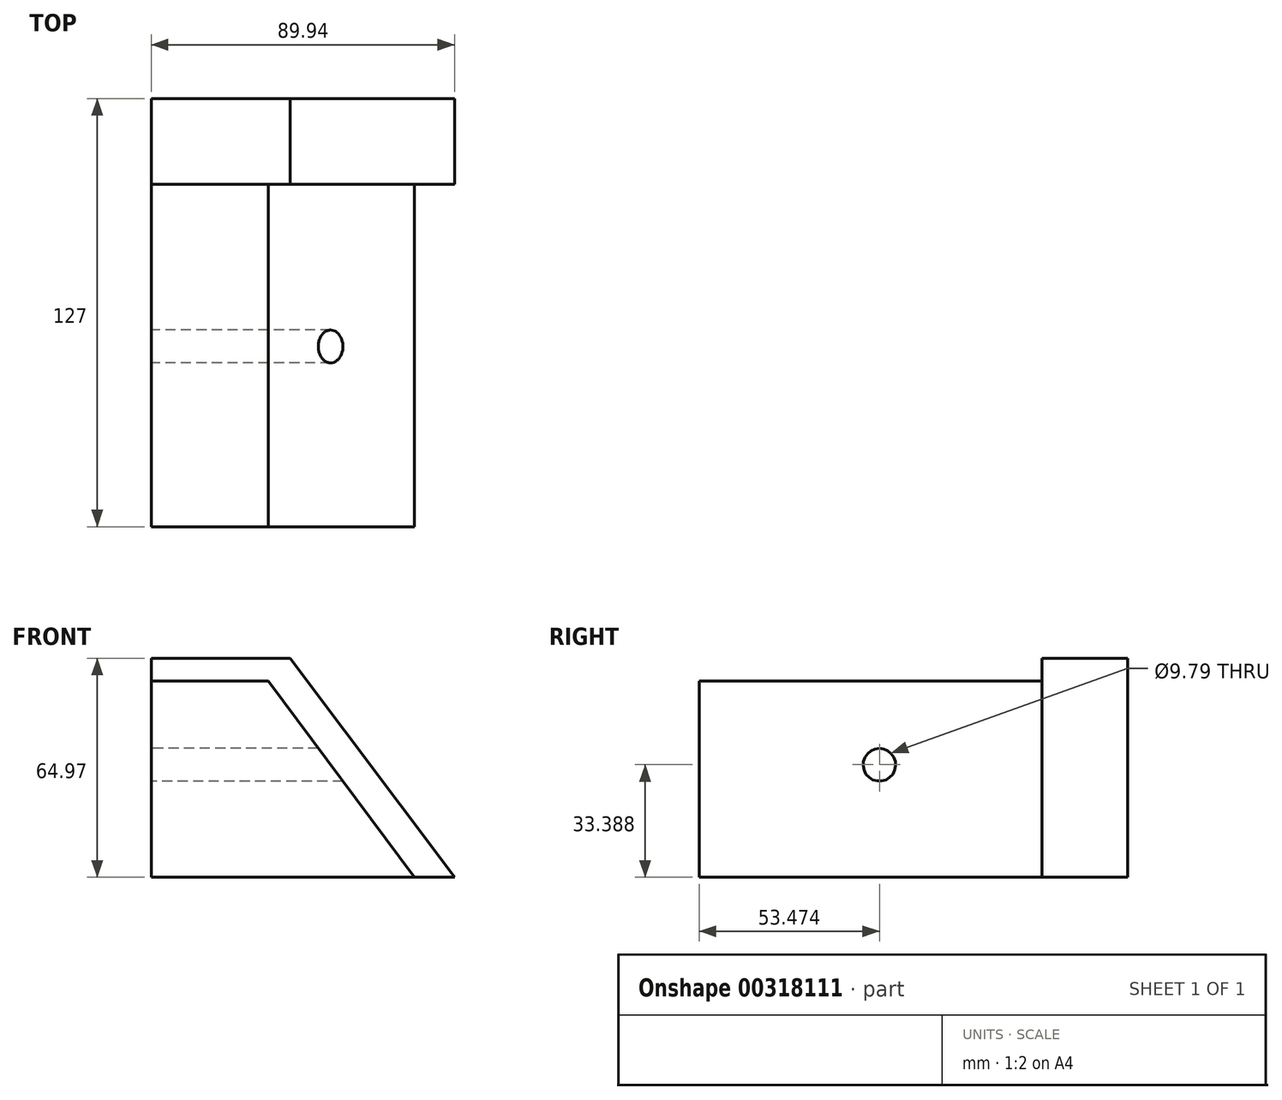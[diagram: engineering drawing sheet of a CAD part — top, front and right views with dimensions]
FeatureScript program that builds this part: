
annotation { "Feature Type Name" : "Feature", "Feature Type Description" : "" }
export const myFeature = defineFeature(function(context is Context, id is Id, definition is map)
    precondition{}
    {
        {
            var Q0;
            Q0=qCreatedBy(makeId("Front.planeOp"),FACE);
            var sketch = newSketch(context, id + "F0", { "sketchPlane" : qUnion([Q0])});
            skLineSegment(sketch, "E0.bottom", {"start": v(-64.07, 0) * mm, "end": v(25.87, 0) * mm});
            skLineSegment(sketch, "E0.top", {"start": v(-64.07, 64.97) * mm, "end": v(-22.86, 64.97) * mm});
            skLineSegment(sketch, "E0.left", {"start": v(-64.07, 0) * mm, "end": v(-64.07, 64.97) * mm});
            skLineSegment(sketch, "E1", {"start": v(25.87, 0) * mm, "end": v(-22.86, 64.97) * mm});
            skSolve(sketch);
        }
        {
            var Q0;
            Q0 = qSketchRegion(id + "F0", true);
            extrude(context, id + "F1", {"entities" : qUnion([Q0]), "depth" : 25.4 * mm});
        }
        {
            var Q0;
            Q0=makeQuery(id+"F1.opExtrude","CAP_FACE",FACE,{"disambiguationData":[OSD([sQuery(id+"F0.wireOp",EDGE,"E0.bottom"),sQuery(id+"F0.wireOp",EDGE,"E0.top"),sQuery(id+"F0.wireOp",EDGE,"E0.left"),sQuery(id+"F0.wireOp",EDGE,"E1")])],"isStart":false});
            var sketch = newSketch(context, id + "F2", { "sketchPlane" : qUnion([Q0])});
            skLineSegment(sketch, "E2.bottom", {"start": v(-64.07, 0) * mm, "end": v(13.95, 0) * mm});
            skLineSegment(sketch, "E2.top", {"start": v(-64.07, 58.27) * mm, "end": v(-29.37, 58.27) * mm});
            skLineSegment(sketch, "E2.left", {"start": v(-64.07, 0) * mm, "end": v(-64.07, 58.27) * mm});
            skLineSegment(sketch, "E3", {"start": v(13.95, 0) * mm, "end": v(-29.37, 58.27) * mm});
            skSolve(sketch);
        }
        {
            var Q0;
            Q0 = qSketchRegion(id + "F2", true);
            extrude(context, id + "F3", {"entities" : qUnion([Q0]), "operationType" : NewBodyOperationType.ADD, "depth" : 101.6 * mm});
        }
        {
            var Q0;
            Q0=makeQuery(id+"F3.boolean.opBoolean","MERGE",FACE,{"derivedFrom":[makeQuery(id+"F1.opExtrude","SWEPT_FACE",FACE,{"disambiguationData":[OSD([sQuery(id+"F0.wireOp",EDGE,"E0.left")])]}),makeQuery(id+"F3.opExtrude","SWEPT_FACE",FACE,{"disambiguationData":[OSD([sQuery(id+"F2.wireOp",EDGE,"E2.left")])]})]});
            var sketch = newSketch(context, id + "F4", { "sketchPlane" : qUnion([Q0])});
            skCircle(sketch, "E4", {"center": v(73.53, 33.39) * mm, "radius": 4.9 * mm});
            skSolve(sketch);
        }
        {
            var Q0;
            Q0 = qSketchRegion(id + "F4", true);
            extrude(context, id + "F5", {"entities" : qUnion([Q0]), "operationType" : NewBodyOperationType.REMOVE, "oppositeDirection" : true, "depth" : 127 * mm});
        }
    });
